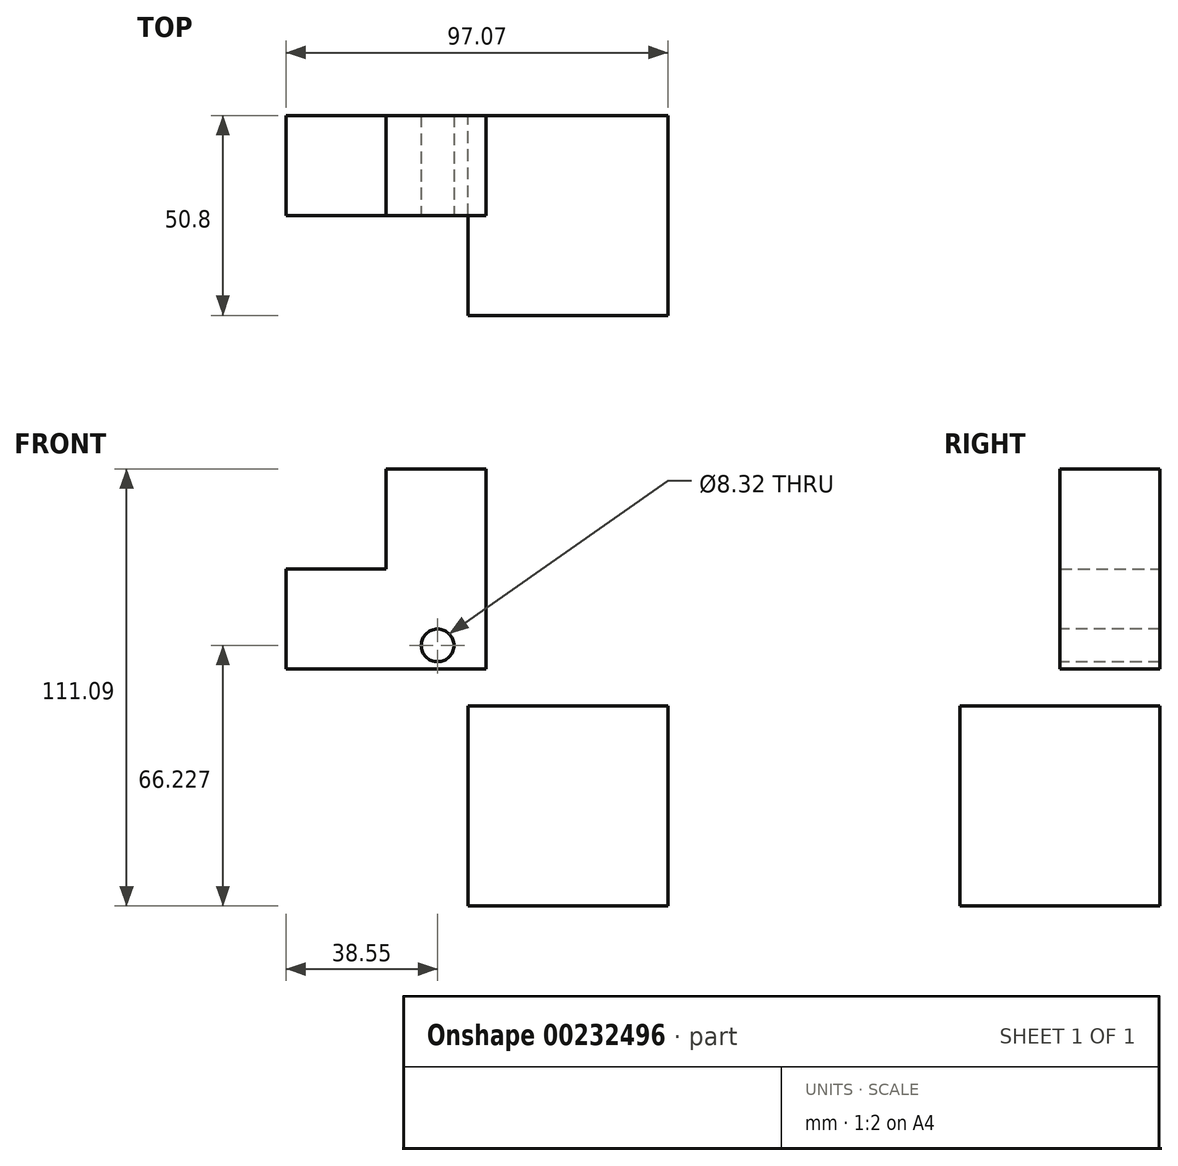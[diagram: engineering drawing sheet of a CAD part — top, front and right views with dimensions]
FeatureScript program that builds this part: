
annotation { "Feature Type Name" : "Feature", "Feature Type Description" : "" }
export const myFeature = defineFeature(function(context is Context, id is Id, definition is map)
    precondition{}
    {
        {
            var Q0;
            Q0=qCreatedBy(makeId("Front.planeOp"),FACE);
            var sketch = newSketch(context, id + "F0", { "sketchPlane" : qUnion([Q0])});
            skLineSegment(sketch, "E0.bottom", {"start": v(-25.4, 25.4) * mm, "end": v(25.4, 25.4) * mm});
            skLineSegment(sketch, "E0.top", {"start": v(-25.4, -25.4) * mm, "end": v(25.4, -25.4) * mm});
            skLineSegment(sketch, "E0.left", {"start": v(-25.4, 25.4) * mm, "end": v(-25.4, -25.4) * mm});
            skLineSegment(sketch, "E0.right", {"start": v(25.4, 25.4) * mm, "end": v(25.4, -25.4) * mm});
            skPoint(sketch, "E0.middle", {"position": v(0, 0) * mm});
            skSolve(sketch);
        }
        {
            var Q0;
            Q0=makeQuery(id+"F0.imprint","IMPRINT",FACE,{"disambiguationData":[TD([[makeQuery(id+"F0.imprint","IMPRINT",EDGE,{"derivedFrom":sQuery(id+"F0.wireOp",EDGE,"E0.bottom")}),-1.0]])]});
            extrude(context, id + "F1", {"entities" : qUnion([Q0]), "depth" : 50.8 * mm});
        }
        {
            var Q0;
            Q0=qCreatedBy(makeId("Front.planeOp"),FACE);
            var sketch = newSketch(context, id + "F2", { "sketchPlane" : qUnion([Q0])});
            skLineSegment(sketch, "E1", {"start": v(-71.67, 60.3) * mm, "end": v(-71.67, 34.9) * mm});
            skLineSegment(sketch, "E2", {"start": v(-71.67, 34.9) * mm, "end": v(-20.87, 34.9) * mm});
            skLineSegment(sketch, "E3", {"start": v(-20.87, 34.9) * mm, "end": v(-20.87, 85.7) * mm});
            skLineSegment(sketch, "E4", {"start": v(-20.87, 85.7) * mm, "end": v(-46.27, 85.7) * mm});
            skLineSegment(sketch, "E5", {"start": v(-46.27, 85.7) * mm, "end": v(-46.27, 60.3) * mm});
            skLineSegment(sketch, "E6", {"start": v(-46.27, 60.3) * mm, "end": v(-71.67, 60.3) * mm});
            skSolve(sketch);
        }
        {
            var Q0;
            Q0=makeQuery(id+"F2.imprint","IMPRINT",FACE,{"disambiguationData":[TD([[makeQuery(id+"F2.imprint","IMPRINT",EDGE,{"derivedFrom":sQuery(id+"F2.wireOp",EDGE,"E1")}),1.0]])]});
            extrude(context, id + "F3", {"entities" : qUnion([Q0]), "depth" : 25.4 * mm});
        }
        {
            var Q0;
            Q0=makeQuery(id+"F3.opExtrude","CAP_FACE",FACE,{"disambiguationData":[OSD([sQuery(id+"F2.wireOp",EDGE,"E1"),sQuery(id+"F2.wireOp",EDGE,"E2"),sQuery(id+"F2.wireOp",EDGE,"E3"),sQuery(id+"F2.wireOp",EDGE,"E4"),sQuery(id+"F2.wireOp",EDGE,"E5"),sQuery(id+"F2.wireOp",EDGE,"E6")])],"isStart":false});
            var sketch = newSketch(context, id + "F4", { "sketchPlane" : qUnion([Q0])});
            skCircle(sketch, "E7", {"center": v(-33.12, 40.83) * mm, "radius": 4.56 * mm});
            skCircle(sketch, "E8", {"center": v(-33.12, 40.83) * mm, "radius": 4.16 * mm});
            skSolve(sketch);
        }
        {
            var Q0;
            Q0=makeQuery(id+"F4.imprint","IMPRINT",FACE,{"disambiguationData":[TD([[makeQuery(id+"F4.imprint","IMPRINT",EDGE,{"derivedFrom":sQuery(id+"F4.wireOp",EDGE,"E8")}),1.0]])]});
            extrude(context, id + "F5", {"entities" : qUnion([Q0]), "operationType" : NewBodyOperationType.REMOVE, "oppositeDirection" : true, "depth" : 75.95 * mm});
        }
    });
